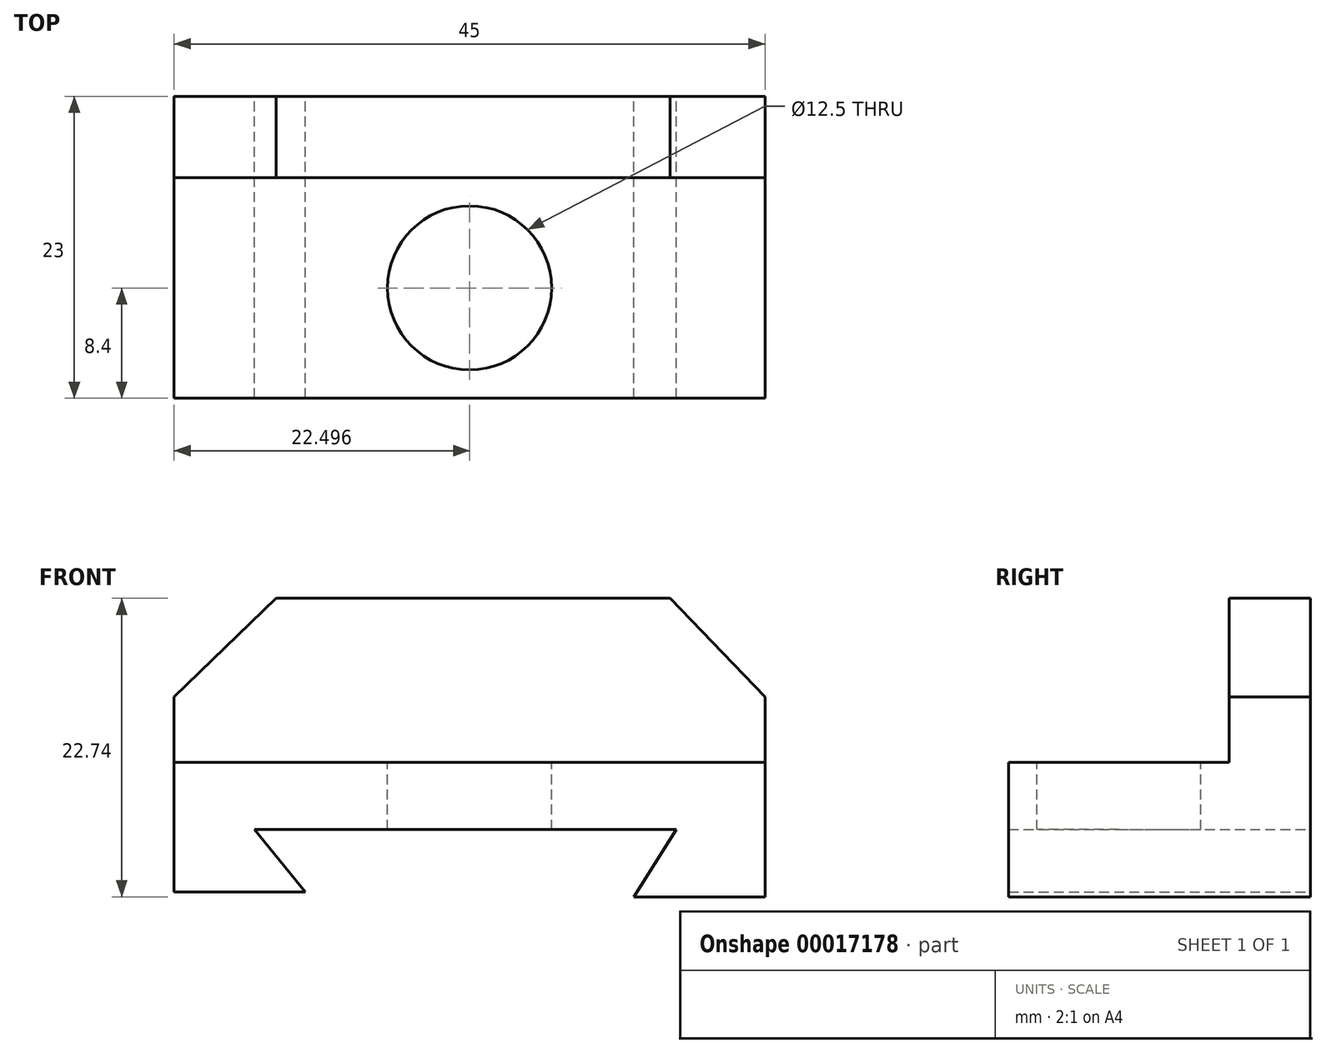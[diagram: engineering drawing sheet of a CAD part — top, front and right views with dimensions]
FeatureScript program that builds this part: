
annotation { "Feature Type Name" : "Feature", "Feature Type Description" : "" }
export const myFeature = defineFeature(function(context is Context, id is Id, definition is map)
    precondition{}
    {
        {
            var Q0;
            Q0=qCreatedBy(makeId("Front.planeOp"),FACE);
            var sketch = newSketch(context, id + "F0", { "sketchPlane" : qUnion([Q0])});
            skLineSegment(sketch, "E0", {"start": v(-35.27, -13.27) * mm, "end": v(-35.27, -23.15) * mm});
            skLineSegment(sketch, "E1", {"start": v(-35.27, -13.27) * mm, "end": v(9.73, -13.27) * mm});
            skLineSegment(sketch, "E2", {"start": v(9.73, -13.27) * mm, "end": v(9.73, -23.5) * mm});
            skLineSegment(sketch, "E3", {"start": v(9.73, -23.5) * mm, "end": v(-0.27, -23.5) * mm});
            skLineSegment(sketch, "E4", {"start": v(-0.27, -23.5) * mm, "end": v(2.96, -18.39) * mm});
            skLineSegment(sketch, "E5", {"start": v(2.96, -18.39) * mm, "end": v(-29.16, -18.39) * mm});
            skLineSegment(sketch, "E6", {"start": v(-35.27, -23.15) * mm, "end": v(-25.27, -23.15) * mm});
            skLineSegment(sketch, "E7", {"start": v(-29.16, -18.39) * mm, "end": v(-25.27, -23.15) * mm});
            skSolve(sketch);
        }
        {
            var Q0;
            Q0 = qSketchRegion(id + "F0", true);
            extrude(context, id + "F1", {"entities" : qUnion([Q0]), "depth" : 23 * mm});
        }
        {
            var Q0;
            Q0=makeQuery(id+"F1.opExtrude","SWEPT_FACE",FACE,{"disambiguationData":[OSD([sQuery(id+"F0.wireOp",EDGE,"E1")])]});
            var sketch = newSketch(context, id + "F2", { "sketchPlane" : qUnion([Q0])});
            skLineSegment(sketch, "E8.bottom", {"start": v(-35.27, 0) * mm, "end": v(9.73, 0) * mm});
            skLineSegment(sketch, "E8.top", {"start": v(-35.27, -6.2) * mm, "end": v(9.73, -6.2) * mm});
            skLineSegment(sketch, "E8.left", {"start": v(-35.27, 0) * mm, "end": v(-35.27, -6.2) * mm});
            skLineSegment(sketch, "E8.right", {"start": v(9.73, 0) * mm, "end": v(9.73, -6.2) * mm});
            skSolve(sketch);
        }
        {
            var Q0;
            Q0 = qSketchRegion(id + "F2", true);
            extrude(context, id + "F3", {"entities" : qUnion([Q0]), "operationType" : NewBodyOperationType.ADD, "depth" : 12.5 * mm});
        }
        {
            var Q0;
            Q0=makeQuery(id+"F3.opExtrude","SWEPT_FACE",FACE,{"disambiguationData":[OSD([sQuery(id+"F2.wireOp",EDGE,"E8.top")])]});
            var sketch = newSketch(context, id + "F4", { "sketchPlane" : qUnion([Q0])});
            skLineSegment(sketch, "E9", {"start": v(-35.27, -0.77) * mm, "end": v(-35.27, -8.27) * mm});
            skLineSegment(sketch, "E10", {"start": v(-35.27, -8.27) * mm, "end": v(-27.5, -0.77) * mm});
            skLineSegment(sketch, "E11", {"start": v(-35.27, -0.77) * mm, "end": v(-27.5, -0.77) * mm});
            skLineSegment(sketch, "E12", {"start": v(9.73, -8.27) * mm, "end": v(9.73, -0.77) * mm});
            skLineSegment(sketch, "E13", {"start": v(2.37, -0.77) * mm, "end": v(9.73, -8.27) * mm});
            skLineSegment(sketch, "E14.bottom", {"start": v(-27.5, -0.77) * mm, "end": v(2.5, -0.77) * mm});
            skSolve(sketch);
        }
        {
            var Q0;
            Q0 = qSketchRegion(id + "F4", true);
            extrude(context, id + "F5", {"entities" : qUnion([Q0]), "operationType" : NewBodyOperationType.REMOVE, "oppositeDirection" : true, "depth" : 25 * mm});
        }
        {
            var Q0;
            Q0=makeQuery(id+"F3.opExtrude","SWEPT_FACE",FACE,{"disambiguationData":[OSD([sQuery(id+"F2.wireOp",EDGE,"E8.top")])]});
            var sketch = newSketch(context, id + "F6", { "sketchPlane" : qUnion([Q0])});
            skLineSegment(sketch, "E15", {"start": v(2.5, -0.77) * mm, "end": v(9.73, -8.27) * mm});
            skLineSegment(sketch, "E16", {"start": v(9.73, -0.77) * mm, "end": v(2.5, -0.77) * mm});
            skSolve(sketch);
        }
        {
            var Q0;
            {var subQ1=sQuery(id+"F6.wireOp",EDGE,"E15");Q0=makeQuery(id+"F6.imprint","IMPRINT",FACE,{"disambiguationData":[TD([[makeQuery(id+"F6.imprint","IMPRINT",EDGE,{"derivedFrom":subQ1}),1.0]])]});}
            extrude(context, id + "F7", {"entities" : qUnion([Q0]), "operationType" : NewBodyOperationType.REMOVE, "oppositeDirection" : true, "depth" : 25 * mm});
        }
        {
            var Q0;
            Q0=makeQuery(id+"F1.opExtrude","SWEPT_FACE",FACE,{"disambiguationData":[OSD([sQuery(id+"F0.wireOp",EDGE,"E1")])]});
            var sketch = newSketch(context, id + "F8", { "sketchPlane" : qUnion([Q0])});
            skCircle(sketch, "E17", {"center": v(-12.77, -14.6) * mm, "radius": 6.66 * mm});
            skSolve(sketch);
        }
        {
            var Q0;
            Q0=sQuery(id+"F8.wireOp",VERTEX,"E17.center");
            var Q1;
            Q1=makeQuery(id+"F1.opExtrude","SWEPT_BODY",BODY,{"disambiguationData":[OSD([sQuery(id+"F0.wireOp",EDGE,"E0"),sQuery(id+"F0.wireOp",EDGE,"E1"),sQuery(id+"F0.wireOp",EDGE,"E2"),sQuery(id+"F0.wireOp",EDGE,"E3"),sQuery(id+"F0.wireOp",EDGE,"E4"),sQuery(id+"F0.wireOp",EDGE,"E5"),sQuery(id+"F0.wireOp",EDGE,"E6"),sQuery(id+"F0.wireOp",EDGE,"E7")])]});
            hole(context, id + "F9", {"style" : HoleStyle.SIMPLE, "holeDiameter" : 12.5 * mm, "endStyle" : HoleEndStyle.THROUGH, "locations" : qUnion([Q0]), "scope" : qUnion([Q1])});
        }
    });
